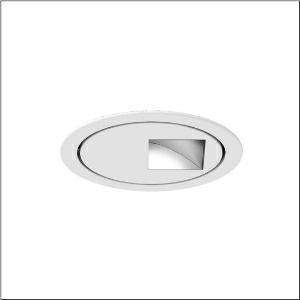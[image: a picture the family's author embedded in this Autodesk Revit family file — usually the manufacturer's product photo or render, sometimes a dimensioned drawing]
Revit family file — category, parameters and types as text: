
# Revit family: lunis_11_mini_round_51dk11b72wf21
name_source: partatom
category: Lighting Fixtures
units: mm (PartAtom-declared; Revit-internal decimal feet)

## family parameters
Cut with Voids When Loaded = No
Host = Face
Light Source = No
Part Type = Normal
Room Calculation Point = No
Round Connector Dimension = Use Diameter
Shared = No

## types (1)
- Lunis 11 mini round (1 x LED 3000K / CRI = 80 (unbekannt), 2380 lm, 3000K)
    Apparent Load = 28 VA
    CIE Flux Codes = 44 77 97 100 100
    Color Rendering = 80
    Color Temperature = 3000K
    Default Elevation = 1800 mm
    Description = Lunis 11 mini round, downlight, light control with wallwasher, of highly reflective aluminium, highly specular, light emission: direct distribution, LED rated luminous flux: 2.380lm, light colour: 830, control gear: ECG, with terminal, 3-pole, mains connection: 220..230V, AC/DC, 0/50..60Hz, LED module, luminaire module, of aluminium, highly specular, white, diameter: 176mm, clamping range: 1..40mm, recessing ring, of plastic, traffic white (RAL 9016), protection rating (complete): IP20, insulation class (complete): insulation class II (safety insulation), certification: CE, permissible ambient temperature for indoor applications: 0..+35°C, packaging unit: 1 piece
    Height = 0 mm  [stored 0 ft]
    Lamp = 1 x LED 3000K / CRI >= 80 (unbekannt)
    Lamp Light Flux = 2380 lm
    Lamp count = 1
    Length = 176 mm
    Luminous efficacy = 85 lm/W
    Manufacturer = Siteco
    ModVariant = No
    Model = 51DK11B72WF21
    Mounting Place = Ceiling
    Mounting Type = Recessed
    Number of Poles = 1
    OnlyDefault = Yes
    Power Factor = 1
    Product Name = Lunis 11 mini round
    Product group = downlight
    ProductGroupID = 401
    Protection Class = Protection class II
    Protection Degree = IP 20
    RLX_Detail_Level = 1
    RLX_Emergency_Light_Flux = 0 lm
    RLX_Emergency_Type = 0
    RLX_Emergency_Type_DB = No
    RlxData = <blob elided: 59205 chars, md5=837ca8f1>
    Socket = socket
    Standby Power = 0 W
    System Light Flux = 2380 lm
    System Power = 28 W
    Type Comments = Product without accessories
    Type Image = l_1004772.jpg
    URL = http://relux.com
    VarID = ---
    Voltage = 0 V
    Weight = 0.00 kg
    Width = 176 mm

note: [stored X ft] marks values corroborated as IEEE doubles in the binary element streams (Revit-internal decimal feet)

## geometry (parser evidence)
native form markers: Blend x4, Sweep x11
no freeform markers — native parametric forms only
